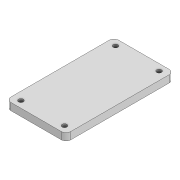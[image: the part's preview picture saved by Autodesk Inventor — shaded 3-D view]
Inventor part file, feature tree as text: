
AUTODESK INVENTOR PART (.ipt)
format: ipt  version: 2020 (Build 240168000, 168)  size: 99,328 bytes
history: native  units: mm
features: extrude x1, fillet x1, sketch x1
ambient origin geometry x8: Origin, YZ Plane, XZ Plane, XY Plane, X Axis, Y Axis, Z Axis, Center Point
bodies: Solid1 (feature_tree)
feature tree (3):
  extrude  "Extrusion1"  Depth=2.0mm
  fillet  "Fillet1"  Radius=2.0mm
  sketch  "Sketch1"  dims[d0=39.5mm d1=18.2mm d2=2.0mm d3=2.0mm d4=2.0mm d5=2.0mm d6=45.0mm d7=25.0mm d8=3.0mm d9=0.0mm d10=2.0mm]
